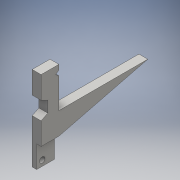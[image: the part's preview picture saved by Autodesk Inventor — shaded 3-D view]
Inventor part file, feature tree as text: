
AUTODESK INVENTOR PART (.ipt)
format: ipt  version: 2016 (Build 200138000, 138)  size: 148,992 bytes
history: native  units: mm
features: extrude x7, sketch x7, other x1
ambient origin geometry x8: Origin, YZ Plane, XZ Plane, XY Plane, X Axis, Y Axis, Z Axis, Center Point
bodies: Body1 (feature_tree)
feature tree (15):
  other  "ソリッド1"
  extrude  "押し出し1"  Depth=4.0mm
  extrude  "押し出し2"  Depth=30.0mm
  extrude  "押し出し6"  Depth=8.0mm TaperAngle=0.0deg
  extrude  "押し出し7"  Depth=5.0mm
  extrude  "押し出し8"  Depth=3.0mm
  extrude  "押し出し9"  Depth=2.0mm
  extrude  "押し出し10"  Depth=10.0mm
  sketch  "スケッチ1"
  sketch  "スケッチ2"
  sketch  "スケッチ6"
  sketch  "スケッチ7"
  sketch  "スケッチ9"
  sketch  "スケッチ10"
  sketch  "スケッチ11"
